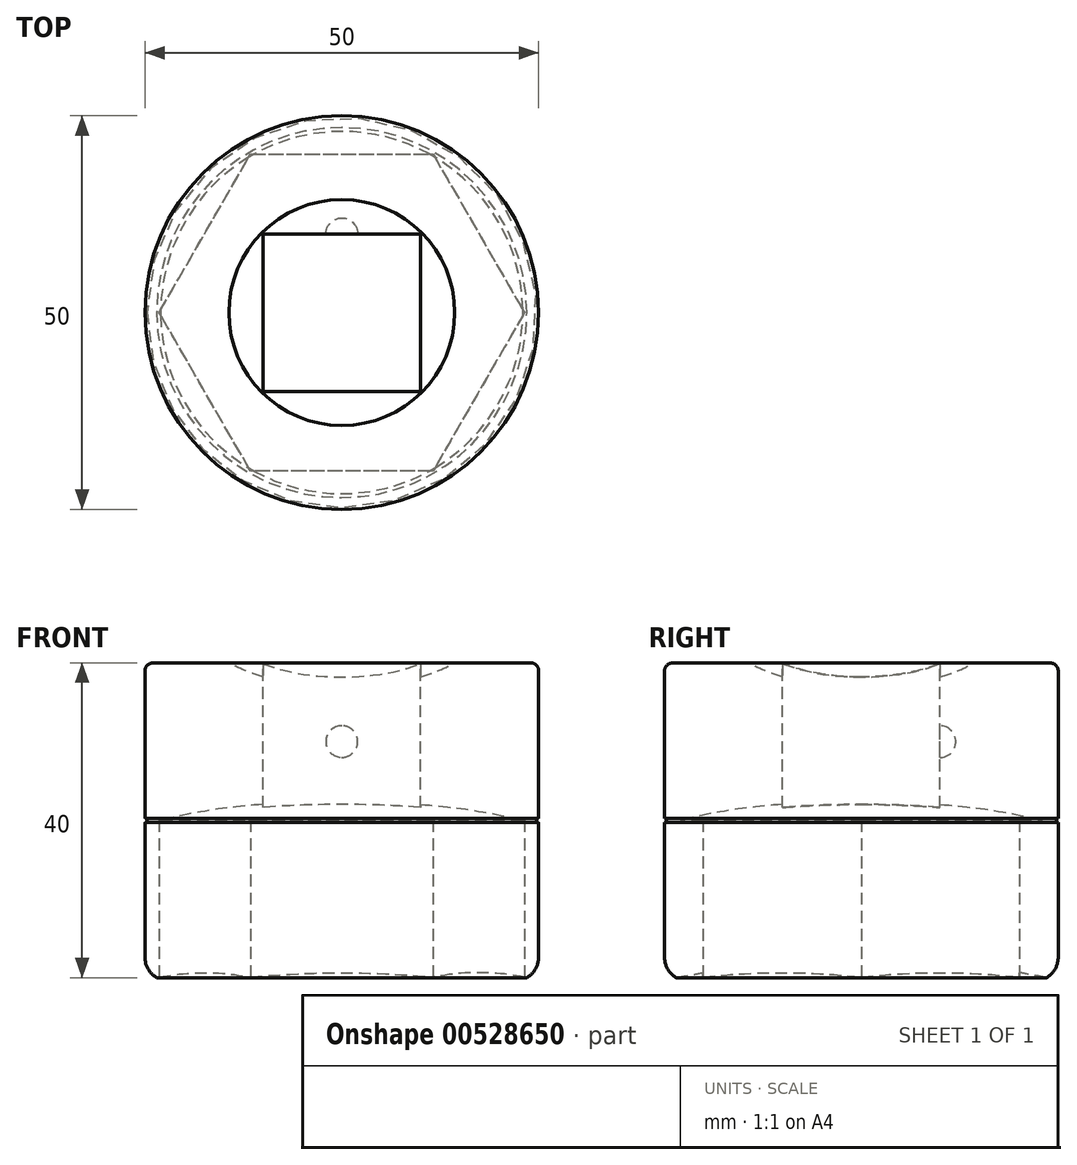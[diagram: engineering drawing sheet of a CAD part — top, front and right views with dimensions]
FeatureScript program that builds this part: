
annotation { "Feature Type Name" : "Feature", "Feature Type Description" : "" }
export const myFeature = defineFeature(function(context is Context, id is Id, definition is map)
    precondition{}
    {
        {
            var Q0;
            Q0=qCreatedBy(makeId("Top.planeOp"),FACE);
            var sketch = newSketch(context, id + "F0", { "sketchPlane" : qUnion([Q0])});
            skCircle(sketch, "E0.cCircle", {"center": v(0, 0) * mm, "radius": 20.1 * mm, "construction": true});
            skLineSegment(sketch, "E0.0", {"start": v(-11.6, 20.1) * mm, "end": v(11.6, 20.1) * mm});
            skLineSegment(sketch, "E0.1", {"start": v(11.6, 20.1) * mm, "end": v(23.2, 0) * mm});
            skLineSegment(sketch, "E0.2", {"start": v(23.2, 0) * mm, "end": v(11.6, -20.1) * mm});
            skLineSegment(sketch, "E0.3", {"start": v(11.6, -20.1) * mm, "end": v(-11.6, -20.1) * mm});
            skLineSegment(sketch, "E0.4", {"start": v(-11.6, -20.1) * mm, "end": v(-23.2, 0) * mm});
            skLineSegment(sketch, "E0.5", {"start": v(-23.2, 0) * mm, "end": v(-11.6, 20.1) * mm});
            skPoint(sketch, "E0.0.midPoint", {"position": v(0, 20.1) * mm});
            skLineSegment(sketch, "E1", {"start": v(0, 0) * mm, "end": v(0, 20.1) * mm});
            skSolve(sketch);
        }
        {
            var Q0;
            Q0=qCreatedBy(makeId("Top.planeOp"),FACE);
            var sketch = newSketch(context, id + "F1", { "sketchPlane" : qUnion([Q0])});
            skCircle(sketch, "E2", {"center": v(0, 0) * mm, "radius": 25 * mm});
            skSolve(sketch);
        }
        {
            var Q0;
            Q0=makeQuery(id+"F1.imprint","IMPRINT",FACE,{"disambiguationData":[TD([[makeQuery(id+"F1.imprint","IMPRINT",EDGE,{"derivedFrom":sQuery(id+"F1.wireOp",EDGE,"E2")}),1.0]])]});
            extrude(context, id + "F2", {"entities" : qUnion([Q0]), "depth" : 40 * mm, "offsetDistance" : 25 * mm});
        }
        {
            var Q0;
            Q0=makeQuery(id+"F0.imprint","IMPRINT",FACE,{"disambiguationData":[TD([[makeQuery(id+"F0.imprint","IMPRINT",EDGE,{"derivedFrom":sQuery(id+"F0.wireOp",EDGE,"E0.0")}),-1.0]])]});
            extrude(context, id + "F3", {"entities" : qUnion([Q0]), "operationType" : NewBodyOperationType.REMOVE, "depth" : 20 * mm, "offsetDistance" : 25 * mm});
        }
        {
            var Q0;
            Q0=makeQuery(id+"F2.opExtrude","CAP_FACE",FACE,{"disambiguationData":[OSD([sQuery(id+"F1.wireOp",EDGE,"E2")])],"isStart":false});
            var sketch = newSketch(context, id + "F4", { "sketchPlane" : qUnion([Q0])});
            skCircle(sketch, "E3.cCircle", {"center": v(0, 0) * mm, "radius": 10 * mm, "construction": true});
            skLineSegment(sketch, "E3.0", {"start": v(10, 10) * mm, "end": v(10, -10) * mm});
            skLineSegment(sketch, "E3.1", {"start": v(10, -10) * mm, "end": v(-10, -10) * mm});
            skLineSegment(sketch, "E3.2", {"start": v(-10, -10) * mm, "end": v(-10, 10) * mm});
            skLineSegment(sketch, "E3.3", {"start": v(-10, 10) * mm, "end": v(10, 10) * mm});
            skPoint(sketch, "E3.0.midPoint", {"position": v(10, 0) * mm});
            skSolve(sketch);
        }
        {
            var Q0;
            Q0=makeQuery(id+"F4.imprint","IMPRINT",FACE,{"disambiguationData":[TD([[makeQuery(id+"F4.imprint","IMPRINT",EDGE,{"derivedFrom":sQuery(id+"F4.wireOp",EDGE,"E3.0")}),-1.0]])]});
            extrude(context, id + "F5", {"entities" : qUnion([Q0]), "operationType" : NewBodyOperationType.REMOVE, "oppositeDirection" : true, "depth" : 21 * mm, "offsetDistance" : 25 * mm});
        }
        {
            var Q0;
            Q0=qCreatedBy(makeId("Front.planeOp"),FACE);
            var sketch = newSketch(context, id + "F6", { "sketchPlane" : qUnion([Q0])});
            skLineSegment(sketch, "E4", {"start": v(0, 0) * mm, "end": v(-23.5, 0) * mm});
            skLineSegment(sketch, "E5", {"start": v(0, 0) * mm, "end": v(0, 2) * mm});
            skArc(sketch, "E6", {"start": v(0, 2) * mm, "mid": v(-11.8, 1.7) * mm, "end": v(-23.5, 0) * mm});
            skSolve(sketch);
        }
        {
            var Q0;
            Q0=qCreatedBy(makeId("Top.planeOp"),FACE);
            var sketch = newSketch(context, id + "F7", { "sketchPlane" : qUnion([Q0])});
            skCircle(sketch, "E7", {"center": v(0, 0) * mm, "radius": 8.02 * mm});
            skSolve(sketch);
        }
        {
            var Q0;
            Q0 = qSketchRegion(id + "F6", true);
            var Q1;
            Q1 = qConstructionFilter(qBodyType(qCreatedBy(id + "F7" ,EDGE), BodyType.WIRE), ConstructionObject.NO);
            sweep(context, id + "F8", {"operationType" : NewBodyOperationType.REMOVE, "profiles" : qUnion([Q0]), "path" : qUnion([Q1])});
        }
        {
            var Q0;
            Q0=makeQuery(id+"F2.opExtrude","CAP_EDGE",EDGE,{"disambiguationData":[OSD([sQuery(id+"F1.wireOp",EDGE,"E2")])],"isStart":true});
            fillet(context, id + "F9", {"entities" : qUnion([Q0]), "radius" : 3 * mm, "tangentPropagation" : true, "allowEdgeOverflow" : false});
        }
        {
            var Q0;
            Q0=qCreatedBy(makeId("Front.planeOp"),FACE);
            var sketch = newSketch(context, id + "F10", { "sketchPlane" : qUnion([Q0])});
            skLineSegment(sketch, "E8", {"start": v(0, 0) * mm, "end": v(0, 20) * mm});
            skLineSegment(sketch, "E9", {"start": v(0, 20) * mm, "end": v(-23, 20) * mm});
            skLineSegment(sketch, "E10", {"start": v(0, 20) * mm, "end": v(0, 22) * mm});
            skArc(sketch, "E11", {"start": v(0, 22) * mm, "mid": v(-11.58, 21.9) * mm, "end": v(-23, 20) * mm});
            skSolve(sketch);
        }
        {
            var Q0;
            Q0 = qSketchRegion(id + "F10", true);
            var Q1;
            Q1 = qConstructionFilter(qBodyType(qCreatedBy(id + "F7" ,EDGE), BodyType.WIRE), ConstructionObject.NO);
            sweep(context, id + "F11", {"operationType" : NewBodyOperationType.REMOVE, "profiles" : qUnion([Q0]), "path" : qUnion([Q1])});
        }
        {
            var Q0;
            Q0=qCreatedBy(makeId("Front.planeOp"),FACE);
            var sketch = newSketch(context, id + "F12", { "sketchPlane" : qUnion([Q0])});
            skLineSegment(sketch, "E12", {"start": v(0, 40) * mm, "end": v(14.34, 40) * mm});
            skLineSegment(sketch, "E13", {"start": v(0, 40) * mm, "end": v(0, 38) * mm});
            skArc(sketch, "E14", {"start": v(0, 38) * mm, "mid": v(7.36, 37.66) * mm, "end": v(14.34, 40) * mm});
            skSolve(sketch);
        }
        {
            var Q0;
            Q0 = qSketchRegion(id + "F12", true);
            var Q1;
            Q1 = qConstructionFilter(qBodyType(qCreatedBy(id + "F7" ,EDGE), BodyType.WIRE), ConstructionObject.NO);
            sweep(context, id + "F13", {"operationType" : NewBodyOperationType.REMOVE, "profiles" : qUnion([Q0]), "path" : qUnion([Q1])});
        }
        {
            var Q0;
            Q0=makeQuery(id+"F2.opExtrude","CAP_EDGE",EDGE,{"disambiguationData":[OSD([sQuery(id+"F1.wireOp",EDGE,"E2")])],"isStart":false});
            fillet(context, id + "F14", {"entities" : qUnion([Q0]), "radius" : 1 * mm, "tangentPropagation" : true, "allowEdgeOverflow" : false});
        }
        {
            var Q0;
            Q0=qCreatedBy(makeId("Front.planeOp"),FACE);
            var sketch = newSketch(context, id + "F15", { "sketchPlane" : qUnion([Q0])});
            skLineSegment(sketch, "E15", {"start": v(0, 0) * mm, "end": v(0, 20) * mm});
            skCircle(sketch, "E16", {"center": v(25, 20) * mm, "radius": 0.25 * mm});
            skSolve(sketch);
        }
        {
            var Q0;
            Q0 = qSketchRegion(id + "F15", true);
            var Q1;
            Q1 = qConstructionFilter(qBodyType(qCreatedBy(id + "F7" ,EDGE), BodyType.WIRE), ConstructionObject.NO);
            sweep(context, id + "F16", {"operationType" : NewBodyOperationType.REMOVE, "profiles" : qUnion([Q0]), "path" : qUnion([Q1])});
        }
        {
            var Q0;
            Q0=makeQuery(id+"F5.boolean.opBoolean","COPY",FACE,{"derivedFrom":makeQuery(id+"F5.opExtrude","SWEPT_FACE",FACE,{"disambiguationData":[OSD([sQuery(id+"F4.wireOp",EDGE,"E3.3")])]})});
            var sketch = newSketch(context, id + "F17", { "sketchPlane" : qUnion([Q0])});
            skLineSegment(sketch, "E17", {"start": v(0, 32) * mm, "end": v(0, 28) * mm});
            skArc(sketch, "E18", {"start": v(0, 32) * mm, "mid": v(-2.02, 30) * mm, "end": v(0, 28) * mm});
            skSolve(sketch);
        }
        {
            var Q0;
            Q0=makeQuery(id+"F17.imprint","IMPRINT",FACE,{"disambiguationData":[TD([[makeQuery(id+"F17.imprint","IMPRINT",EDGE,{"derivedFrom":sQuery(id+"F17.wireOp",EDGE,"E17")}),1.0]])]});
            var sketch = newSketch(context, id + "F18", { "sketchPlane" : qUnion([Q0])});
            skLineSegment(sketch, "E19", {"start": v(0, 0) * mm, "end": v(0, 40) * mm});
            skSolve(sketch);
        }
        {
            var Q0;
            Q0 = qSketchRegion(id + "F17", true);
            var Q1;
            Q1=sQuery(id+"F18.wireOp",EDGE,"E19");
            revolve(context, id + "F19", {"operationType" : NewBodyOperationType.REMOVE, "entities" : qUnion([Q0]), "axis" : qUnion([Q1]), "revolveType" : RevolveType.FULL, "oppositeDirection" : true});
        }
    });
